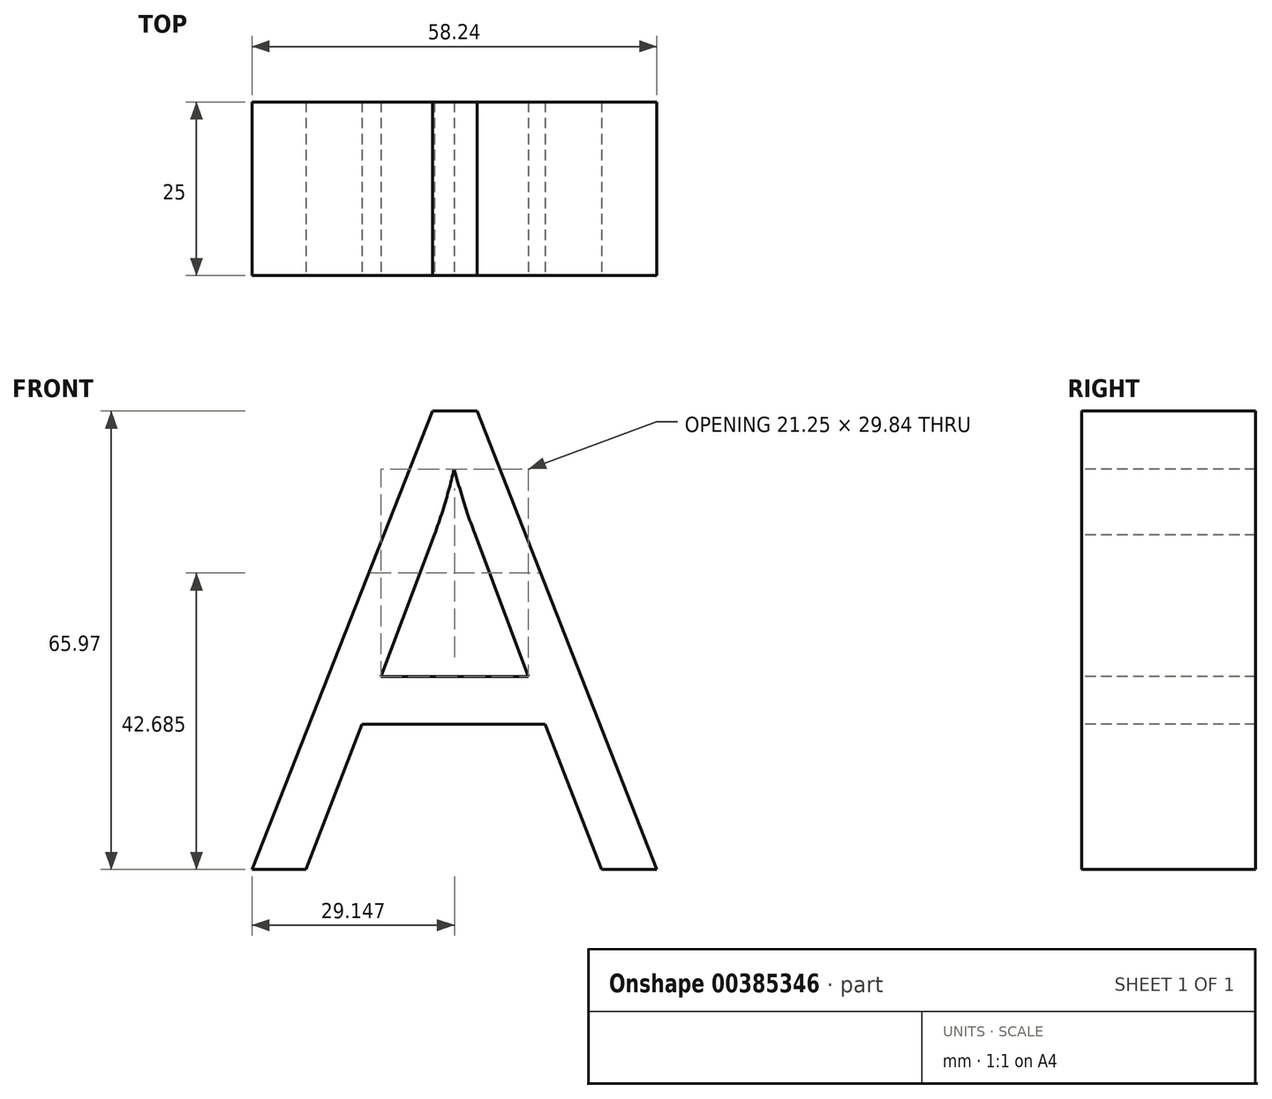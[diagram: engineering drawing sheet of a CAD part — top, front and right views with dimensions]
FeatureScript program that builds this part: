
annotation { "Feature Type Name" : "Feature", "Feature Type Description" : "" }
export const myFeature = defineFeature(function(context is Context, id is Id, definition is map)
    precondition{}
    {
        {
            var Q0;
            Q0=qCreatedBy(makeId("Front.planeOp"),FACE);
            var sketch = newSketch(context, id + "F0", { "sketchPlane" : qUnion([Q0])});
            skText(sketch, "E0", { "text": "A", "fontName": "OpenSans-Regular.ttf"});
            const initialGuessF0  = {"E0": [-0.0436, -0.02523, 1, 0, 0.06626]};
            skSetInitialGuess(sketch, initialGuessF0);
            skSolve(sketch);
        }
        {
            var Q0;
            Q0=qSketchRegion(id+"F0",true);
            extrude(context, id + "F1", {"entities" : qUnion([Q0]), "oppositeDirection" : true, "depth" : 25 * mm});
        }
    });
